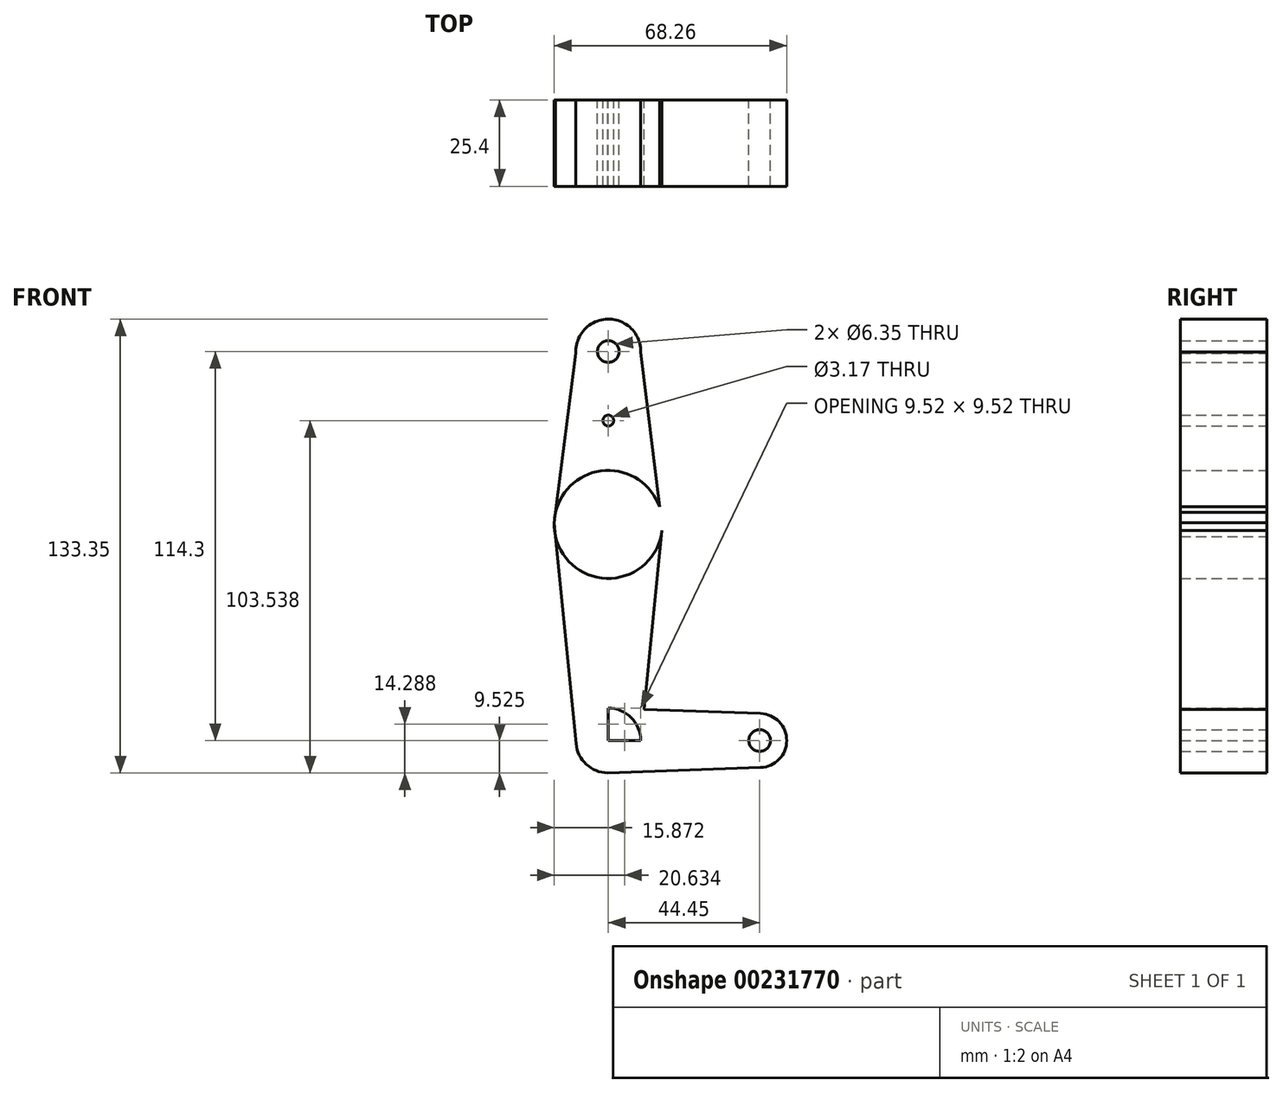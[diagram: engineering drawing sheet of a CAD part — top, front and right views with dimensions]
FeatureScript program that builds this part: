
annotation { "Feature Type Name" : "Feature", "Feature Type Description" : "" }
export const myFeature = defineFeature(function(context is Context, id is Id, definition is map)
    precondition{}
    {
        {
            var Q0;
            Q0=qCreatedBy(makeId("Front.planeOp"),FACE);
            var sketch = newSketch(context, id + "F0", { "sketchPlane" : qUnion([Q0])});
            skLineSegment(sketch, "E0", {"start": v(-37.16, 61.86) * mm, "end": v(-37.16, -52.44) * mm});
            skLineSegment(sketch, "E1", {"start": v(-37.16, -52.44) * mm, "end": v(7.3, -52.44) * mm});
            skCircle(sketch, "E2", {"center": v(-37.16, 61.86) * mm, "radius": 9.53 * mm});
            skCircle(sketch, "E3", {"center": v(-37.16, 11.06) * mm, "radius": 15.88 * mm});
            skCircle(sketch, "E4", {"center": v(-37.16, -52.44) * mm, "radius": 9.53 * mm});
            skCircle(sketch, "E5", {"center": v(7.3, -52.44) * mm, "radius": 7.94 * mm});
            skLineSegment(sketch, "E6", {"start": v(-46.67, 61.29) * mm, "end": v(-53.03, 11.54) * mm});
            skLineSegment(sketch, "E7", {"start": v(-53.03, 11.54) * mm, "end": v(-46.64, -53.38) * mm});
            skLineSegment(sketch, "E8", {"start": v(-21.39, 9.23) * mm, "end": v(-27.59, -52.44) * mm});
            skLineSegment(sketch, "E9", {"start": v(-27.63, 61.7) * mm, "end": v(-22.14, 16.2) * mm});
            skLineSegment(sketch, "E10", {"start": v(-37.16, -42.92) * mm, "end": v(7.57, -44.51) * mm});
            skLineSegment(sketch, "E11", {"start": v(-37.32, -61.97) * mm, "end": v(7.57, -60.38) * mm});
            skCircle(sketch, "E12", {"center": v(-37.16, 41.57) * mm, "radius": 1.59 * mm});
            skCircle(sketch, "E13", {"center": v(-37.16, 61.86) * mm, "radius": 3.18 * mm});
            skCircle(sketch, "E14", {"center": v(7.3, -52.44) * mm, "radius": 3.18 * mm});
            skCircle(sketch, "E15", {"center": v(-37.16, 11.06) * mm, "radius": 3.18 * mm});
            skSolve(sketch);
        }
        {
            var Q0;
            {var subQ0=sQuery(id+"F0.wireOp",EDGE,"E6");var subQ1=sQuery(id+"F0.wireOp",EDGE,"E3");var subQ3=makeQuery(id+"F0.imprint","INTERSECT",VERTEX,{"derivedFrom":[subQ1,subQ0]});Q0=makeQuery(id+"F0.imprint","IMPRINT",FACE,{"disambiguationData":[TD([[makeQuery(id+"F0.imprint","IMPRINT",EDGE,{"disambiguationData":[TD([[subQ3,-1.0]])],"derivedFrom":subQ1}),1.0]])]});}
            var Q1;
            {var subQ0=sQuery(id+"F0.wireOp",EDGE,"E7");var subQ1=sQuery(id+"F0.wireOp",EDGE,"E3");var subQ3=makeQuery(id+"F0.imprint","INTERSECT",VERTEX,{"derivedFrom":[subQ1,subQ0]});Q1=makeQuery(id+"F0.imprint","IMPRINT",FACE,{"disambiguationData":[TD([[makeQuery(id+"F0.imprint","IMPRINT",EDGE,{"disambiguationData":[TD([[subQ3,1.0]])],"derivedFrom":subQ1}),1.0]])]});}
            var Q2;
            {var subQ0=sQuery(id+"F0.wireOp",EDGE,"E11");var subQ1=sQuery(id+"F0.wireOp",EDGE,"E4");var subQ2=makeQuery(id+"F0.imprint","INTERSECT",VERTEX,{"disambiguationData":[OD(0.0)],"derivedFrom":[subQ1,subQ0]});Q2=makeQuery(id+"F0.imprint","IMPRINT",FACE,{"disambiguationData":[TD([[makeQuery(id+"F0.imprint","IMPRINT",EDGE,{"disambiguationData":[TD([[subQ2,-1.0]])],"derivedFrom":subQ1}),1.0]])]});}
            var Q3;
            {var subQ3=sQuery(id+"F0.wireOp",EDGE,"E3");var subQ5=sQuery(id+"F0.wireOp",EDGE,"E7");var subQ6=makeQuery(id+"F0.imprint","INTERSECT",VERTEX,{"derivedFrom":[subQ3,subQ5]});Q3=makeQuery(id+"F0.imprint","IMPRINT",FACE,{"disambiguationData":[TD([[makeQuery(id+"F0.imprint","IMPRINT",EDGE,{"disambiguationData":[TD([[subQ6,-1.0]])],"derivedFrom":subQ3}),-1.0]])]});}
            var Q4;
            {var subQ0=sQuery(id+"F0.wireOp",EDGE,"E8");var subQ1=sQuery(id+"F0.wireOp",EDGE,"E1");var subQ2=makeQuery(id+"F0.imprint","INTERSECT",VERTEX,{"derivedFrom":[subQ1,subQ0]});Q4=makeQuery(id+"F0.imprint","IMPRINT",FACE,{"disambiguationData":[TD([[makeQuery(id+"F0.imprint","IMPRINT",EDGE,{"disambiguationData":[TD([[subQ2,-1.0]])],"derivedFrom":subQ1}),1.0]])]});}
            var Q5;
            Q5=makeQuery(id+"F0.imprint","IMPRINT",FACE,{"disambiguationData":[TD([[makeQuery(id+"F0.imprint","IMPRINT",EDGE,{"derivedFrom":sQuery(id+"F0.wireOp",EDGE,"E13")}),-1.0]])]});
            var Q6;
            Q6=makeQuery(id+"F0.imprint","IMPRINT",FACE,{"disambiguationData":[TD([[makeQuery(id+"F0.imprint","IMPRINT",EDGE,{"derivedFrom":sQuery(id+"F0.wireOp",EDGE,"E14")}),-1.0]])]});
            var Q7;
            {var subQ0=sQuery(id+"F0.wireOp",EDGE,"E9");Q7=makeQuery(id+"F0.imprint","IMPRINT",FACE,{"disambiguationData":[TD([[makeQuery(id+"F0.imprint","IMPRINT",EDGE,{"derivedFrom":subQ0}),-1.0]])]});}
            var Q8;
            {var subQ0=sQuery(id+"F0.wireOp",EDGE,"E3");var subQ2=sQuery(id+"F0.wireOp",EDGE,"E0");var subQ3=makeQuery(id+"F0.imprint","INTERSECT",VERTEX,{"disambiguationData":[OD(0.0)],"derivedFrom":[subQ2,subQ0]});Q8=makeQuery(id+"F0.imprint","IMPRINT",FACE,{"disambiguationData":[TD([[makeQuery(id+"F0.imprint","IMPRINT",EDGE,{"disambiguationData":[TD([[subQ3,-1.0]])],"derivedFrom":subQ2}),1.0]])]});}
            var Q9;
            {var subQ0=sQuery(id+"F0.wireOp",EDGE,"E8");var subQ1=sQuery(id+"F0.wireOp",EDGE,"E3");var subQ2=makeQuery(id+"F0.imprint","INTERSECT",VERTEX,{"derivedFrom":[subQ1,subQ0]});Q9=makeQuery(id+"F0.imprint","IMPRINT",FACE,{"disambiguationData":[TD([[makeQuery(id+"F0.imprint","IMPRINT",EDGE,{"disambiguationData":[TD([[subQ2,1.0]])],"derivedFrom":subQ1}),-1.0]])]});}
            var Q10;
            {var subQ2=sQuery(id+"F0.wireOp",EDGE,"E0");var subQ7=sQuery(id+"F0.wireOp",EDGE,"E1");var subQ8=makeQuery(id+"F0.imprint","INTERSECT",VERTEX,{"derivedFrom":[subQ2,subQ7]});Q10=makeQuery(id+"F0.imprint","IMPRINT",FACE,{"disambiguationData":[TD([[makeQuery(id+"F0.imprint","IMPRINT",EDGE,{"disambiguationData":[TD([[subQ8,-1.0]])],"derivedFrom":subQ7}),-1.0]])]});}
            var Q11;
            {var subQ3=sQuery(id+"F0.wireOp",EDGE,"E1");var subQ8=makeQuery(id+"F0.imprint","INTERSECT",VERTEX,{"derivedFrom":[subQ3,sQuery(id+"F0.wireOp",EDGE,"E8")]});Q11=makeQuery(id+"F0.imprint","IMPRINT",FACE,{"disambiguationData":[TD([[makeQuery(id+"F0.imprint","IMPRINT",EDGE,{"disambiguationData":[TD([[subQ8,1.0]])],"derivedFrom":subQ3}),-1.0]])]});}
            var Q12;
            {var subQ0=sQuery(id+"F0.wireOp",EDGE,"E8");var subQ1=sQuery(id+"F0.wireOp",EDGE,"E1");var subQ2=makeQuery(id+"F0.imprint","INTERSECT",VERTEX,{"derivedFrom":[subQ1,subQ0]});Q12=makeQuery(id+"F0.imprint","IMPRINT",FACE,{"disambiguationData":[TD([[makeQuery(id+"F0.imprint","IMPRINT",EDGE,{"disambiguationData":[TD([[subQ2,1.0]])],"derivedFrom":subQ1}),1.0]])]});}
            var Q13;
            {var subQ1=sQuery(id+"F0.wireOp",EDGE,"E3");var subQ3=sQuery(id+"F0.wireOp",EDGE,"E0");var subQ4=makeQuery(id+"F0.imprint","INTERSECT",VERTEX,{"disambiguationData":[OD(0.0)],"derivedFrom":[subQ3,subQ1]});Q13=makeQuery(id+"F0.imprint","IMPRINT",FACE,{"disambiguationData":[TD([[makeQuery(id+"F0.imprint","IMPRINT",EDGE,{"disambiguationData":[TD([[subQ4,-1.0]])],"derivedFrom":subQ3}),-1.0]])]});}
            var Q14;
            {var subQ0=sQuery(id+"F0.wireOp",EDGE,"E12");var subQ1=sQuery(id+"F0.wireOp",EDGE,"E0");var subQ2=makeQuery(id+"F0.imprint","INTERSECT",VERTEX,{"disambiguationData":[OD(0.0)],"derivedFrom":[subQ1,subQ0]});Q14=makeQuery(id+"F0.imprint","IMPRINT",FACE,{"disambiguationData":[TD([[makeQuery(id+"F0.imprint","IMPRINT",EDGE,{"disambiguationData":[TD([[subQ2,-1.0]])],"derivedFrom":subQ1}),1.0]])]});}
            var Q15;
            {var subQ3=sQuery(id+"F0.wireOp",EDGE,"E0");var subQ5=sQuery(id+"F0.wireOp",EDGE,"E2");var subQ7=makeQuery(id+"F0.imprint","INTERSECT",VERTEX,{"derivedFrom":[subQ3,subQ5]});Q15=makeQuery(id+"F0.imprint","IMPRINT",FACE,{"disambiguationData":[TD([[makeQuery(id+"F0.imprint","IMPRINT",EDGE,{"disambiguationData":[TD([[subQ7,-1.0]])],"derivedFrom":subQ3}),-1.0]])]});}
            extrude(context, id + "F1", {"entities" : qUnion([Q0, Q1, Q2, Q3, Q4, Q5, Q6, Q7, Q8, Q9, Q10, Q11, Q12, Q13, Q14, Q15]), "depth" : 25.4 * mm});
        }
    });
